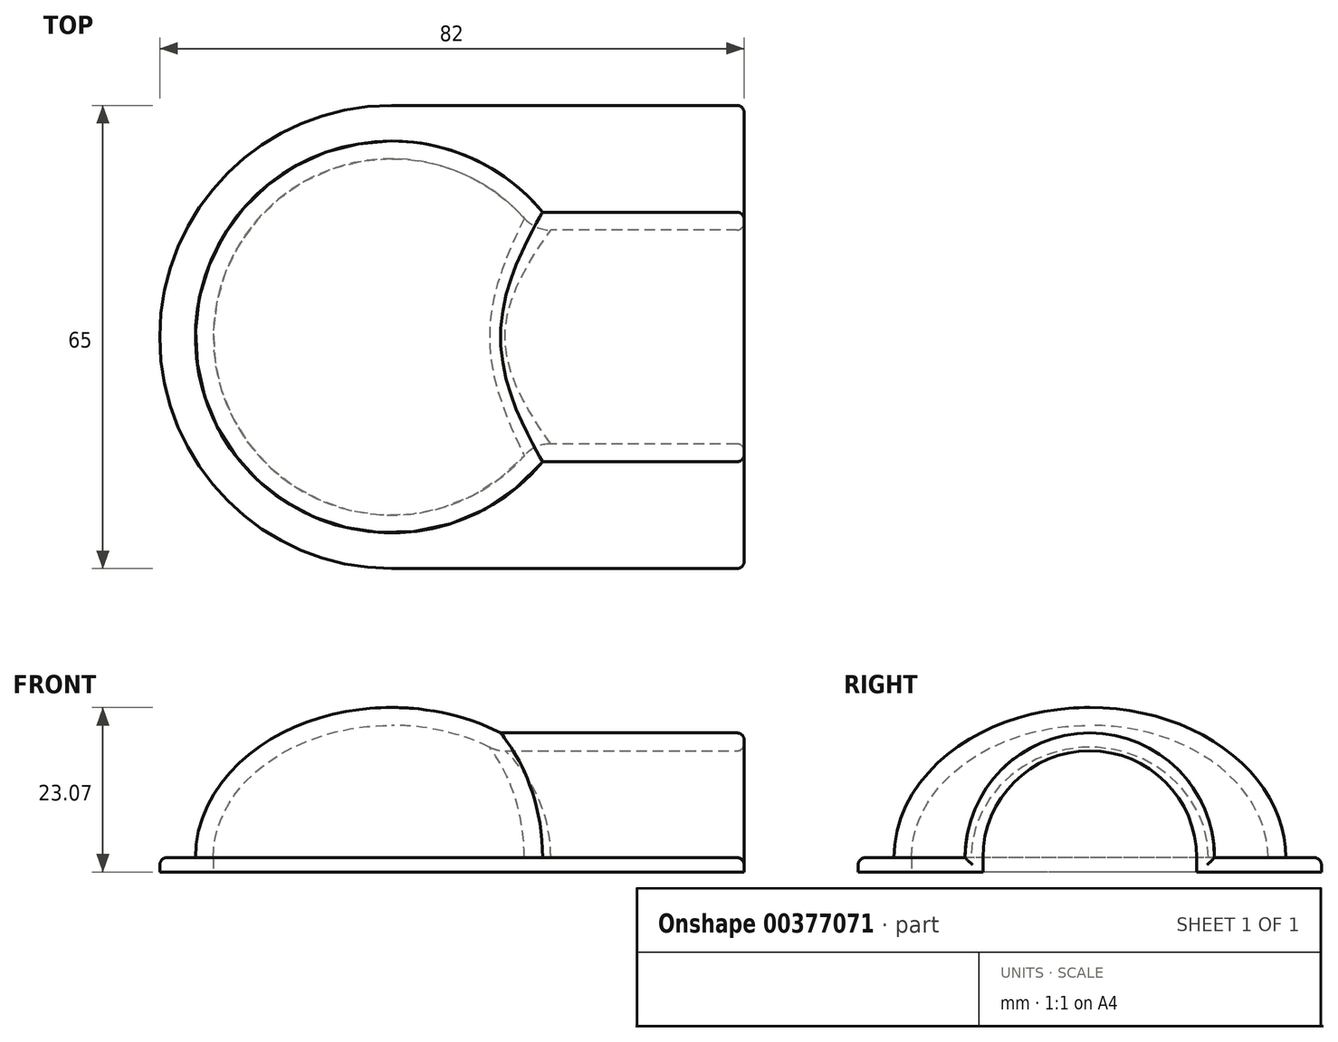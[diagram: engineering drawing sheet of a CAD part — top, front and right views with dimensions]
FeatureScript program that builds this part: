
annotation { "Feature Type Name" : "Feature", "Feature Type Description" : "" }
export const myFeature = defineFeature(function(context is Context, id is Id, definition is map)
    precondition{}
    {
        {
            var Q0;
            Q0=qCreatedBy(makeId("Top.planeOp"),FACE);
            var sketch = newSketch(context, id + "F0", { "sketchPlane" : qUnion([Q0])});
            skLineSegment(sketch, "E0.right", {"start": v(47.5, 15) * mm, "end": v(47.5, -15) * mm});
            skLineSegment(sketch, "E1", {"start": v(0, 0) * mm, "end": v(27.5, 0) * mm, "construction": true});
            skPoint(sketch, "E1.endSnap0", {"position": v(27.5, 0) * mm});
            skPoint(sketch, "E2.startSnap0", {"position": v(47.5, 0) * mm});
            skLineSegment(sketch, "E3", {"start": v(20, 15) * mm, "end": v(20, 15) * mm});
            skArc(sketch, "E4", {"start": v(20, -15) * mm, "mid": v(25, 0) * mm, "end": v(20, 15) * mm, "construction": true});
            skArc(sketch, "E5", {"start": v(20, 15) * mm, "mid": v(-25, 0) * mm, "end": v(20, -15) * mm});
            skLineSegment(sketch, "E6", {"start": v(20, 15) * mm, "end": v(20, -15) * mm});
            skCircle(sketch, "E7", {"center": v(0, 0) * mm, "radius": 32.5 * mm});
            skCircle(sketch, "E8", {"center": v(0, 0) * mm, "radius": 30 * mm});
            skLineSegment(sketch, "E9", {"start": v(0, 32.5) * mm, "end": v(49.5, 32.5) * mm});
            skLineSegment(sketch, "E10", {"start": v(49.5, 32.5) * mm, "end": v(49.5, 15) * mm});
            skLineSegment(sketch, "E11", {"start": v(49.5, 15) * mm, "end": v(20, 15) * mm});
            skLineSegment(sketch, "E12", {"start": v(0, 30) * mm, "end": v(49.5, 30) * mm});
            skLineSegment(sketch, "E13", {"start": v(49.5, 17.5) * mm, "end": v(17.85, 17.5) * mm});
            skLineSegment(sketch, "E14.MirrorCS", {"start": v(49.5, -15) * mm, "end": v(20, -15) * mm});
            skLineSegment(sketch, "E15.MirrorCS", {"start": v(49.5, -17.5) * mm, "end": v(17.85, -17.5) * mm});
            skLineSegment(sketch, "E16.MirrorCS", {"start": v(0, -30) * mm, "end": v(49.5, -30) * mm});
            skLineSegment(sketch, "E17.MirrorCS", {"start": v(0, -32.5) * mm, "end": v(49.5, -32.5) * mm});
            skLineSegment(sketch, "E18.MirrorCS", {"start": v(49.5, -32.5) * mm, "end": v(49.5, -15) * mm});
            skSolve(sketch);
        }
        {
            var Q0;
            {var subQ5=sQuery(id+"F0.wireOp",EDGE,"E7");var subQ8=makeQuery(id+"F0.imprint","INTERSECT",VERTEX,{"derivedFrom":[subQ5,sQuery(id+"F0.wireOp",EDGE,"E9")]});Q0=makeQuery(id+"F0.imprint","IMPRINT",FACE,{"disambiguationData":[TD([[makeQuery(id+"F0.imprint","IMPRINT",EDGE,{"disambiguationData":[TD([[subQ8,1.0]])],"derivedFrom":subQ5}),1.0]])]});}
            var Q1;
            {var subQ4=sQuery(id+"F0.wireOp",EDGE,"E5");var subQ7=sQuery(id+"F0.wireOp",EDGE,"E13");var subQ9=makeQuery(id+"F0.imprint","INTERSECT",VERTEX,{"derivedFrom":[subQ4,subQ7]});Q1=makeQuery(id+"F0.imprint","IMPRINT",FACE,{"disambiguationData":[TD([[makeQuery(id+"F0.imprint","IMPRINT",EDGE,{"disambiguationData":[TD([[subQ9,-1.0]])],"derivedFrom":subQ4}),-1.0]])]});}
            var Q2;
            {var subQ0=sQuery(id+"F0.wireOp",EDGE,"E13");var subQ1=sQuery(id+"F0.wireOp",EDGE,"E7");var subQ2=makeQuery(id+"F0.imprint","INTERSECT",VERTEX,{"derivedFrom":[subQ1,subQ0]});Q2=makeQuery(id+"F0.imprint","IMPRINT",FACE,{"disambiguationData":[TD([[makeQuery(id+"F0.imprint","IMPRINT",EDGE,{"disambiguationData":[TD([[subQ2,-1.0]])],"derivedFrom":subQ1}),1.0]])]});}
            var Q3;
            {var subQ0=sQuery(id+"F0.wireOp",EDGE,"E13");var subQ1=sQuery(id+"F0.wireOp",EDGE,"E7");var subQ2=makeQuery(id+"F0.imprint","INTERSECT",VERTEX,{"derivedFrom":[subQ1,subQ0]});Q3=makeQuery(id+"F0.imprint","IMPRINT",FACE,{"disambiguationData":[TD([[makeQuery(id+"F0.imprint","IMPRINT",EDGE,{"disambiguationData":[TD([[subQ2,-1.0]])],"derivedFrom":subQ1}),-1.0]])]});}
            var Q4;
            {var subQ2=sQuery(id+"F0.wireOp",EDGE,"E7");var subQ6=sQuery(id+"F0.wireOp",EDGE,"E13");var subQ8=makeQuery(id+"F0.imprint","INTERSECT",VERTEX,{"derivedFrom":[subQ2,subQ6]});Q4=makeQuery(id+"F0.imprint","IMPRINT",FACE,{"disambiguationData":[TD([[makeQuery(id+"F0.imprint","IMPRINT",EDGE,{"disambiguationData":[TD([[subQ8,1.0]])],"derivedFrom":subQ2}),-1.0]])]});}
            var Q5;
            {var subQ0=sQuery(id+"F0.wireOp",EDGE,"E13");var subQ1=sQuery(id+"F0.wireOp",EDGE,"E7");var subQ2=makeQuery(id+"F0.imprint","INTERSECT",VERTEX,{"derivedFrom":[subQ1,subQ0]});Q5=makeQuery(id+"F0.imprint","IMPRINT",FACE,{"disambiguationData":[TD([[makeQuery(id+"F0.imprint","IMPRINT",EDGE,{"disambiguationData":[TD([[subQ2,1.0]])],"derivedFrom":subQ1}),1.0]])]});}
            var Q6;
            {var subQ3=sQuery(id+"F0.wireOp",EDGE,"E13");var subQ5=sQuery(id+"F0.wireOp",EDGE,"E8");var subQ7=makeQuery(id+"F0.imprint","INTERSECT",VERTEX,{"derivedFrom":[subQ5,subQ3]});Q6=makeQuery(id+"F0.imprint","IMPRINT",FACE,{"disambiguationData":[TD([[makeQuery(id+"F0.imprint","IMPRINT",EDGE,{"disambiguationData":[TD([[subQ7,1.0]])],"derivedFrom":subQ5}),1.0]])]});}
            var Q7;
            {var subQ3=sQuery(id+"F0.wireOp",EDGE,"E15.MirrorCS");var subQ5=sQuery(id+"F0.wireOp",EDGE,"E8");var subQ6=makeQuery(id+"F0.imprint","INTERSECT",VERTEX,{"derivedFrom":[subQ5,subQ3]});Q7=makeQuery(id+"F0.imprint","IMPRINT",FACE,{"disambiguationData":[TD([[makeQuery(id+"F0.imprint","IMPRINT",EDGE,{"disambiguationData":[TD([[subQ6,-1.0]])],"derivedFrom":subQ5}),1.0]])]});}
            var Q8;
            {var subQ0=sQuery(id+"F0.wireOp",EDGE,"E15.MirrorCS");var subQ1=sQuery(id+"F0.wireOp",EDGE,"E7");var subQ2=makeQuery(id+"F0.imprint","INTERSECT",VERTEX,{"derivedFrom":[subQ1,subQ0]});Q8=makeQuery(id+"F0.imprint","IMPRINT",FACE,{"disambiguationData":[TD([[makeQuery(id+"F0.imprint","IMPRINT",EDGE,{"disambiguationData":[TD([[subQ2,-1.0]])],"derivedFrom":subQ1}),1.0]])]});}
            var Q9;
            {var subQ2=sQuery(id+"F0.wireOp",EDGE,"E7");var subQ4=sQuery(id+"F0.wireOp",EDGE,"E15.MirrorCS");var subQ5=makeQuery(id+"F0.imprint","INTERSECT",VERTEX,{"derivedFrom":[subQ2,subQ4]});Q9=makeQuery(id+"F0.imprint","IMPRINT",FACE,{"disambiguationData":[TD([[makeQuery(id+"F0.imprint","IMPRINT",EDGE,{"disambiguationData":[TD([[subQ5,-1.0]])],"derivedFrom":subQ2}),-1.0]])]});}
            var Q10;
            {var subQ0=sQuery(id+"F0.wireOp",EDGE,"E9");Q10=makeQuery(id+"F0.imprint","IMPRINT",FACE,{"disambiguationData":[TD([[makeQuery(id+"F0.imprint","IMPRINT",EDGE,{"derivedFrom":subQ0}),-1.0]])]});}
            var Q11;
            {var subQ0=sQuery(id+"F0.wireOp",EDGE,"E17.MirrorCS");Q11=makeQuery(id+"F0.imprint","IMPRINT",FACE,{"disambiguationData":[TD([[makeQuery(id+"F0.imprint","IMPRINT",EDGE,{"derivedFrom":subQ0}),1.0]])]});}
            var Q12;
            {var subQ0=sQuery(id+"F0.wireOp",EDGE,"E16.MirrorCS");var subQ1=sQuery(id+"F0.wireOp",EDGE,"E7");var subQ2=makeQuery(id+"F0.imprint","INTERSECT",VERTEX,{"derivedFrom":[subQ1,subQ0]});Q12=makeQuery(id+"F0.imprint","IMPRINT",FACE,{"disambiguationData":[TD([[makeQuery(id+"F0.imprint","IMPRINT",EDGE,{"disambiguationData":[TD([[subQ2,-1.0]])],"derivedFrom":subQ1}),-1.0]])]});}
            var Q13;
            {var subQ0=sQuery(id+"F0.wireOp",EDGE,"E16.MirrorCS");var subQ1=sQuery(id+"F0.wireOp",EDGE,"E7");var subQ2=makeQuery(id+"F0.imprint","INTERSECT",VERTEX,{"derivedFrom":[subQ1,subQ0]});Q13=makeQuery(id+"F0.imprint","IMPRINT",FACE,{"disambiguationData":[TD([[makeQuery(id+"F0.imprint","IMPRINT",EDGE,{"disambiguationData":[TD([[subQ2,-1.0]])],"derivedFrom":subQ1}),1.0]])]});}
            var Q14;
            {var subQ0=sQuery(id+"F0.wireOp",EDGE,"E0.right");Q14=makeQuery(id+"F0.imprint","IMPRINT",FACE,{"disambiguationData":[TD([[makeQuery(id+"F0.imprint","IMPRINT",EDGE,{"derivedFrom":subQ0}),-1.0]])]});}
            var Q15;
            Q15=sQuery(id+"F0.wireOp",EDGE,"j9GyygJ6-EQdW-RxHO-nqTD-LDnlb5gnC7yc.right");
            extrude(context, id + "F1", {"entities" : qUnion([Q0, Q1, Q2, Q3, Q4, Q5, Q6, Q7, Q8, Q9, Q10, Q11, Q12, Q13, Q14]), "surfaceEntities" : qUnion([Q15]), "depth" : 2 * mm});
        }
        {
            var Q0;
            Q0=makeQuery(id+"F1.opExtrude","SWEPT_FACE",FACE,{"disambiguationData":[OSD([sQuery(id+"F0.wireOp",EDGE,"E0.right")])]});
            var sketch = newSketch(context, id + "F2", { "sketchPlane" : qUnion([Q0])});
            skLineSegment(sketch, "E19.left", {"start": v(-17.5, 0) * mm, "end": v(-17.5, 2) * mm});
            skArc(sketch, "E20", {"start": v(17.5, 2) * mm, "mid": v(0, 19.5) * mm, "end": v(-17.5, 2) * mm});
            skLineSegment(sketch, "E21.0", {"start": v(15, 0) * mm, "end": v(-15, 0) * mm});
            skLineSegment(sketch, "E22.0", {"start": v(17.5, 0) * mm, "end": v(-17.5, 0) * mm});
            skLineSegment(sketch, "E23", {"start": v(-15, 2) * mm, "end": v(-17.5, 2) * mm});
            skArc(sketch, "E24", {"start": v(-15, 2) * mm, "mid": v(0, -13) * mm, "end": v(15, 2) * mm, "construction": true});
            skArc(sketch, "E25", {"start": v(15, 2) * mm, "mid": v(0, 17) * mm, "end": v(-15, 2) * mm});
            skLineSegment(sketch, "E26", {"start": v(17.5, 0) * mm, "end": v(17.5, 2) * mm});
            skLineSegment(sketch, "E27", {"start": v(17.5, 2) * mm, "end": v(15, 2) * mm});
            skLineSegment(sketch, "E28", {"start": v(15, 2) * mm, "end": v(15, 0) * mm});
            skLineSegment(sketch, "E29", {"start": v(-15, 0) * mm, "end": v(-15, 2) * mm});
            skLineSegment(sketch, "E30", {"start": v(-15, 2) * mm, "end": v(15, 2) * mm});
            skSolve(sketch);
        }
        {
            var Q0;
            {var subQ0=sQuery(id+"F2.wireOp",EDGE,"E28");Q0=makeQuery(id+"F2.imprint","IMPRINT",FACE,{"disambiguationData":[TD([[makeQuery(id+"F2.imprint","IMPRINT",EDGE,{"derivedFrom":subQ0}),-1.0]])]});}
            cPlane(context, id + "F3", {"entities" : qUnion([Q0]), "cplaneType" : CPlaneType.OFFSET, "offset" : 27.5 * mm, "oppositeDirection" : true, "width" : 150 * mm, "height" : 150 * mm});
        }
        {
            var Q0;
            Q0=qCreatedBy(id+"F3.planeOp",FACE);
            var sketch = newSketch(context, id + "F4", { "sketchPlane" : qUnion([Q0])});
            skLineSegment(sketch, "E31.0.0", {"start": v(-15, -28) * mm, "end": v(15, -28) * mm});
            skLineSegment(sketch, "E31.0.1", {"start": v(15, -28) * mm, "end": v(15, 2) * mm});
            skLineSegment(sketch, "E31.0.2", {"start": v(15, 2) * mm, "end": v(-15, 2) * mm});
            skLineSegment(sketch, "E31.0.3", {"start": v(-15, 2) * mm, "end": v(-15, -28) * mm});
            skArc(sketch, "E32.0", {"start": v(17.5, 2) * mm, "mid": v(0, 19.5) * mm, "end": v(-17.5, 2) * mm});
            skArc(sketch, "E33.0", {"start": v(15, 2) * mm, "mid": v(0, 17) * mm, "end": v(-15, 2) * mm});
            skLineSegment(sketch, "E34.0", {"start": v(-15, 2) * mm, "end": v(-17.5, 2) * mm});
            skLineSegment(sketch, "E34.1", {"start": v(15, 2) * mm, "end": v(17.5, 2) * mm});
            skSolve(sketch);
        }
        {
            var Q0;
            Q0=qCreatedBy(makeId("Right.planeOp"),FACE);
            var sketch = newSketch(context, id + "F5", { "sketchPlane" : qUnion([Q0])});
            skLineSegment(sketch, "E35.0", {"start": v(-25, 2) * mm, "end": v(25, 2) * mm, "construction": true});
            skLineSegment(sketch, "E36", {"start": v(-25, 2) * mm, "end": v(-27.5, 2) * mm});
            skLineSegment(sketch, "E37", {"start": v(25, 2) * mm, "end": v(27.5, 2) * mm});
            skLineSegment(sketch, "E38", {"start": v(0, 2) * mm, "end": v(0, -9.36) * mm, "construction": true});
            skPoint(sketch, "E38.endSnap0", {"position": v(0, 2) * mm});
            skEllipticalArc(sketch, "E39", {});
            skEllipticalArc(sketch, "E40", {"construction": true});
            skEllipticalArc(sketch, "E41", {});
            skEllipticalArc(sketch, "E42", {"construction": true});
            skEllipticalArc(sketch, "E43", {"construction": true});
            skLineSegment(sketch, "E44", {"start": v(0, 23.07) * mm, "end": v(0, 23.07) * mm});
            skEllipticalArc(sketch, "E45", {"construction": true});
            skLineSegment(sketch, "E46.0", {"start": v(-25, 2) * mm, "end": v(25, 2) * mm});
            skLineSegment(sketch, "E47", {"start": v(0, 2) * mm, "end": v(0.7, 8.4) * mm, "construction": true});
            skLineSegment(sketch, "E48", {"start": v(0, 20.57) * mm, "end": v(0, 23.07) * mm});
            const initialGuessF5  = {"E39": [0, 0.002, -1, 0, 0.025, 0.018571428571428558, 3.141592653589793, 4.71238898038469], "E40": [0, 0.002, -1, 0, 0.025, 0.018571428571428558, 0, 3.141592653589793], "E41": [0, 0.002, 1, 0, 0.0275, 0.02107142857142856, 0, 1.5707963267948966], "E42": [0, 0.002, 1, 0, 0.0275, 0.02107142857142856, 3.141592653589793, 0], "E43": [0, 0.002, -1, 0, 0.025, 0.018571428571428558, 4.71238898038469, 0], "E45": [0, 0.002, 1, 0, 0.0275, 0.02107142857142856, 1.5707963267948966, 3.141592653589793]};
            skSetInitialGuess(sketch, initialGuessF5);
            skSolve(sketch);
        }
        {
            var Q0;
            Q0=makeQuery(id+"F5.imprint","IMPRINT",FACE,{"disambiguationData":[TD([[makeQuery(id+"F5.imprint","IMPRINT",EDGE,{"derivedFrom":sQuery(id+"F5.wireOp",EDGE,"E37")}),1.0]])]});
            var Q1;
            Q1=sQuery(id+"F5.wireOp",EDGE,"9d03f4fb-2774-41a7-9f28-2867fa488a81");
            var Q2;
            Q2=sQuery(id+"F5.wireOp",EDGE,"43d41c3b-ab51-473e-acb4-36b242d12c4a");
            var Q3;
            Q3=sQuery(id+"F5.wireOp",EDGE,"NrZWXsPh-ITAb-Np38-96s4-Fa4cZL1205oR");
            var Q4;
            Q4=sQuery(id+"F5.wireOp",EDGE,"dbc90979-7252-4fe3-9eb8-df7eaed7a4aa");
            var Q5;
            Q5=sQuery(id+"F5.wireOp",EDGE,"E38");
            revolve(context, id + "F6", {"operationType" : NewBodyOperationType.ADD, "entities" : qUnion([Q0]), "surfaceEntities" : qUnion([Q1, Q2, Q3, Q4]), "axis" : qUnion([Q5]), "revolveType" : RevolveType.FULL});
        }
        {
            var Q0;
            Q0=makeQuery(id+"F2.imprint","IMPRINT",FACE,{"disambiguationData":[TD([[makeQuery(id+"F2.imprint","IMPRINT",EDGE,{"derivedFrom":sQuery(id+"F2.wireOp",EDGE,"E20")}),1.0]])]});
            var Q1;
            Q1=makeQuery(id+"F1.opExtrude","SWEPT_BODY",BODY,{"disambiguationData":[OSD([sQuery(id+"F0.wireOp",EDGE,"E0.right"),sQuery(id+"F0.wireOp",EDGE,"E5"),sQuery(id+"F0.wireOp",EDGE,"E7"),sQuery(id+"F0.wireOp",EDGE,"E9"),sQuery(id+"F0.wireOp",EDGE,"E10"),sQuery(id+"F0.wireOp",EDGE,"E11"),sQuery(id+"F0.wireOp",EDGE,"E14.MirrorCS"),sQuery(id+"F0.wireOp",EDGE,"E17.MirrorCS"),sQuery(id+"F0.wireOp",EDGE,"E18.MirrorCS")])]});
            extrude(context, id + "F7", {"entities" : qUnion([Q0]), "operationType" : NewBodyOperationType.ADD, "endBound" : BoundingType.UP_TO_NEXT, "oppositeDirection" : true, "endBoundEntityBody" : qUnion([Q1]), "depth" : 25 * mm});
        }
        {
            var Q0;
            Q0=makeQuery(id+"F4.imprint","IMPRINT",FACE,{"disambiguationData":[TD([[makeQuery(id+"F4.imprint","IMPRINT",EDGE,{"derivedFrom":sQuery(id+"F4.wireOp",EDGE,"E31.0.2")}),-1.0]])]});
            extrude(context, id + "F8", {"entities" : qUnion([Q0]), "operationType" : NewBodyOperationType.REMOVE, "oppositeDirection" : true, "depth" : 40 * mm, "symmetric" : true});
        }
        {
            var Q0;
            {var subQ0=sQuery(id+"F2.wireOp",EDGE,"E28");Q0=makeQuery(id+"F2.imprint","IMPRINT",FACE,{"disambiguationData":[TD([[makeQuery(id+"F2.imprint","IMPRINT",EDGE,{"derivedFrom":subQ0}),-1.0]])]});}
            var Q1;
            Q1=qCreatedBy(id+"F3.planeOp",FACE);
            extrude(context, id + "F9", {"entities" : qUnion([Q0]), "operationType" : NewBodyOperationType.REMOVE, "endBound" : BoundingType.UP_TO_SURFACE, "oppositeDirection" : true, "endBoundEntityFace" : qUnion([Q1]), "depth" : 3 * mm});
        }
        {
            var Q0;
            Q0=makeQuery(id+"F2.imprint","IMPRINT",FACE,{"disambiguationData":[TD([[makeQuery(id+"F2.imprint","IMPRINT",EDGE,{"derivedFrom":sQuery(id+"F2.wireOp",EDGE,"E20")}),1.0]])]});
            extrude(context, id + "F10", {"entities" : qUnion([Q0]), "operationType" : NewBodyOperationType.ADD, "depth" : 2 * mm});
        }
        {
            var Q0;
            Q0=makeQuery(id+"F1.opExtrude","SWEPT_EDGE",EDGE,{"disambiguationData":[OSD([sQuery(id+"F0.wireOp",EDGE,"E17.MirrorCS"),sQuery(id+"F0.wireOp",EDGE,"E18.MirrorCS")])]});
            var Q1;
            Q1=makeQuery(id+"F1.opExtrude","SWEPT_EDGE",EDGE,{"disambiguationData":[OSD([sQuery(id+"F0.wireOp",EDGE,"E9"),sQuery(id+"F0.wireOp",EDGE,"E10")])]});
            var Q2;
            Q2=makeQuery(id+"F1.opExtrude","SWEPT_EDGE",EDGE,{"disambiguationData":[OSD([sQuery(id+"F0.wireOp",EDGE,"E10"),sQuery(id+"F0.wireOp",EDGE,"E11")])]});
            var Q3;
            Q3=makeQuery(id+"F1.opExtrude","CAP_EDGE",EDGE,{"disambiguationData":[OSD([sQuery(id+"F0.wireOp",EDGE,"E18.MirrorCS")])],"isStart":false});
            var Q4;
            Q4=makeQuery(id+"F10.opExtrude","CAP_EDGE",EDGE,{"disambiguationData":[OSD([sQuery(id+"F2.wireOp",EDGE,"E20")])],"isStart":false});
            var Q5;
            Q5=makeQuery(id+"F1.opExtrude","CAP_EDGE",EDGE,{"disambiguationData":[OSD([sQuery(id+"F0.wireOp",EDGE,"E10")])],"isStart":false});
            var Q6;
            Q6=makeQuery(id+"F1.opExtrude","CAP_EDGE",EDGE,{"disambiguationData":[OSD([sQuery(id+"F0.wireOp",EDGE,"E9")])],"isStart":false});
            fillet(context, id + "F11", {"entities" : qUnion([Q0, Q1, Q2, Q3, Q4, Q5, Q6]), "radius" : 1 * mm, "tangentPropagation" : true, "allowEdgeOverflow" : false});
        }
        {
            var Q0;
            Q0=makeQuery(id+"F1.opExtrude","SWEPT_EDGE",EDGE,{"disambiguationData":[OSD([sQuery(id+"F0.wireOp",EDGE,"E5"),sQuery(id+"F0.wireOp",EDGE,"E6"),sQuery(id+"F0.wireOp",EDGE,"E14.MirrorCS")])]});
            fillet(context, id + "F12", {"entities" : qUnion([Q0]), "radius" : 5 * mm, "tangentPropagation" : true, "allowEdgeOverflow" : false});
        }
    });
